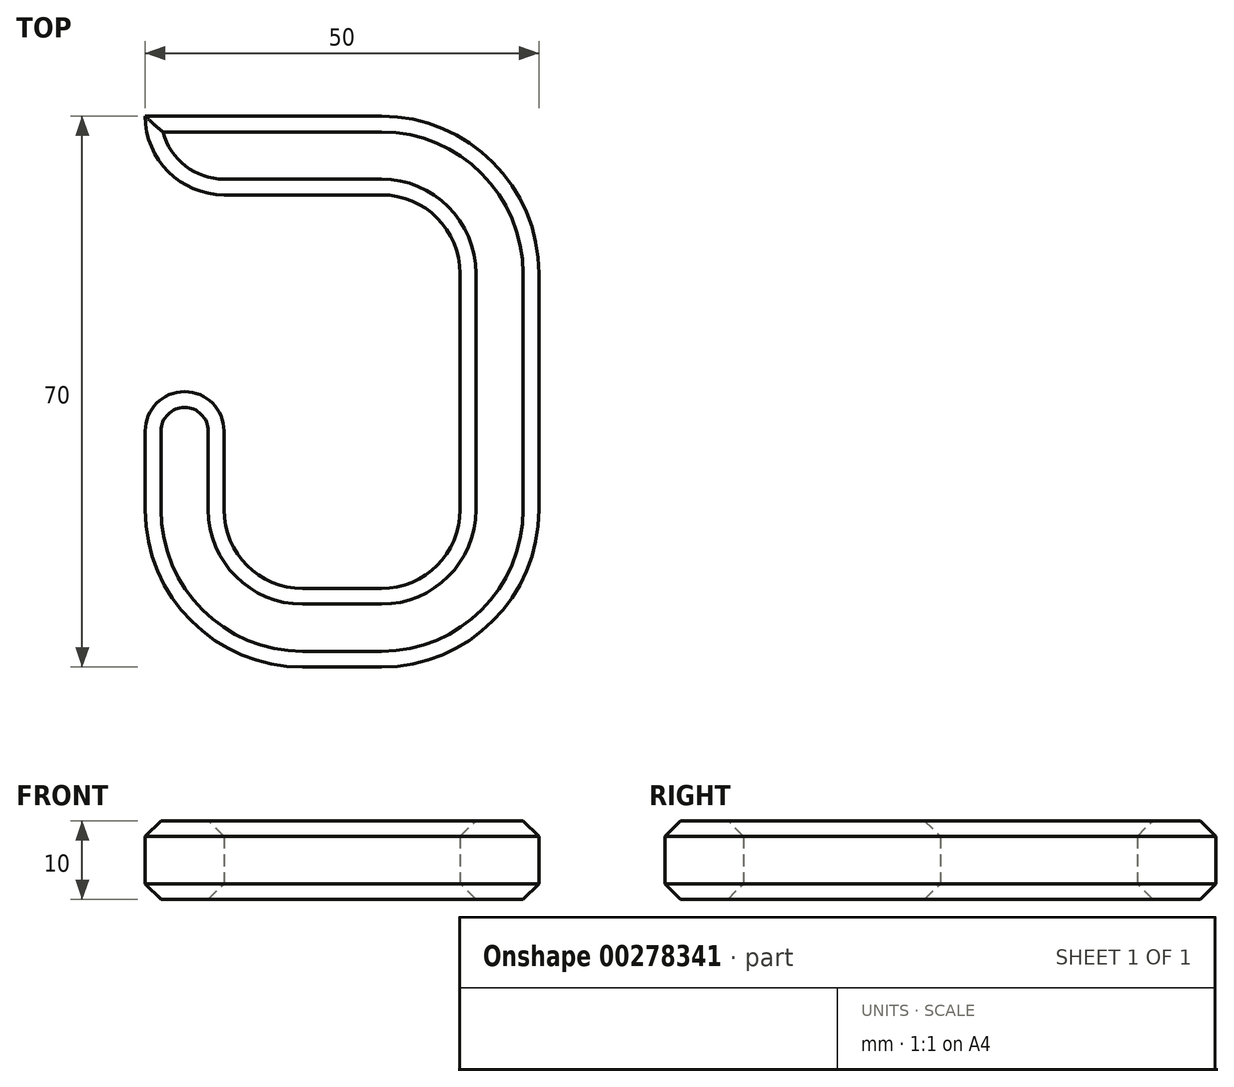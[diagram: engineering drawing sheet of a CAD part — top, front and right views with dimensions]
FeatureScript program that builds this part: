
annotation { "Feature Type Name" : "Feature", "Feature Type Description" : "" }
export const myFeature = defineFeature(function(context is Context, id is Id, definition is map)
    precondition{}
    {
        {
            var Q0;
            Q0=qCreatedBy(makeId("Top.planeOp"),FACE);
            var sketch = newSketch(context, id + "F0", { "sketchPlane" : qUnion([Q0])});
            skLineSegment(sketch, "E0.bottom", {"start": v(-5, 25) * mm, "end": v(5, 25) * mm});
            skLineSegment(sketch, "E0.top", {"start": v(-5, -25) * mm, "end": v(5, -25) * mm});
            skLineSegment(sketch, "E0.left", {"start": v(-5, 25) * mm, "end": v(-5, -25) * mm});
            skLineSegment(sketch, "E0.right", {"start": v(5, 25) * mm, "end": v(5, -25) * mm});
            skPoint(sketch, "E0.middle", {"position": v(0, 0) * mm});
            skLineSegment(sketch, "E1.bottom", {"start": v(-45, 35) * mm, "end": v(5, 35) * mm});
            skLineSegment(sketch, "E1.top", {"start": v(-45, 25) * mm, "end": v(5, 25) * mm});
            skLineSegment(sketch, "E1.left", {"start": v(-45, 35) * mm, "end": v(-45, 25) * mm});
            skLineSegment(sketch, "E1.right", {"start": v(5, 35) * mm, "end": v(5, 25) * mm});
            skLineSegment(sketch, "E2.bottom", {"start": v(-45, -35) * mm, "end": v(5, -35) * mm});
            skLineSegment(sketch, "E2.top", {"start": v(-45, -25) * mm, "end": v(5, -25) * mm});
            skLineSegment(sketch, "E2.left", {"start": v(-45, -35) * mm, "end": v(-45, -25) * mm});
            skLineSegment(sketch, "E2.right", {"start": v(5, -35) * mm, "end": v(5, -25) * mm});
            skLineSegment(sketch, "E3.bottom", {"start": v(-45, 25) * mm, "end": v(-35, 25) * mm});
            skLineSegment(sketch, "E3.top", {"start": v(-45, 10) * mm, "end": v(-35, 10) * mm});
            skLineSegment(sketch, "E3.left", {"start": v(-45, 25) * mm, "end": v(-45, 10) * mm});
            skLineSegment(sketch, "E3.right", {"start": v(-35, 25) * mm, "end": v(-35, 10) * mm});
            skLineSegment(sketch, "E4.bottom", {"start": v(-45, 0) * mm, "end": v(-35, 0) * mm});
            skLineSegment(sketch, "E4.top", {"start": v(-45, -25) * mm, "end": v(-35, -25) * mm});
            skLineSegment(sketch, "E4.left", {"start": v(-45, 0) * mm, "end": v(-45, -25) * mm});
            skLineSegment(sketch, "E4.right", {"start": v(-35, 0) * mm, "end": v(-35, -25) * mm});
            skSolve(sketch);
        }
        {
            var Q0;
            Q0=makeQuery(id+"F0.imprint","IMPRINT",FACE,{"disambiguationData":[TD([[makeQuery(id+"F0.imprint","IMPRINT",EDGE,{"derivedFrom":sQuery(id+"F0.wireOp",EDGE,"E3.bottom")}),-1.0]])]});
            var Q1;
            Q1=makeQuery(id+"F0.imprint","IMPRINT",FACE,{"disambiguationData":[TD([[makeQuery(id+"F0.imprint","IMPRINT",EDGE,{"derivedFrom":sQuery(id+"F0.wireOp",EDGE,"E1.bottom")}),-1.0]])]});
            var Q2;
            {var subQ0=sQuery(id+"F0.wireOp",EDGE,"E0.left");Q2=makeQuery(id+"F0.imprint","IMPRINT",FACE,{"disambiguationData":[TD([[makeQuery(id+"F0.imprint","IMPRINT",EDGE,{"derivedFrom":subQ0}),1.0]])]});}
            var Q3;
            Q3=makeQuery(id+"F0.imprint","IMPRINT",FACE,{"disambiguationData":[TD([[makeQuery(id+"F0.imprint","IMPRINT",EDGE,{"derivedFrom":sQuery(id+"F0.wireOp",EDGE,"E2.bottom")}),1.0]])]});
            var Q4;
            Q4=makeQuery(id+"F0.imprint","IMPRINT",FACE,{"disambiguationData":[TD([[makeQuery(id+"F0.imprint","IMPRINT",EDGE,{"derivedFrom":sQuery(id+"F0.wireOp",EDGE,"E4.bottom")}),-1.0]])]});
            extrude(context, id + "F1", {"entities" : qUnion([Q0, Q1, Q2, Q3, Q4]), "depth" : 10 * mm});
        }
        {
            var Q0;
            Q0=makeQuery(id+"F1.opExtrude","SWEPT_EDGE",EDGE,{"disambiguationData":[OSD([sQuery(id+"F0.wireOp",EDGE,"E1.top"),sQuery(id+"F0.wireOp",EDGE,"E3.bottom"),sQuery(id+"F0.wireOp",EDGE,"E3.right")])]});
            var Q1;
            Q1=makeQuery(id+"F1.opExtrude","SWEPT_EDGE",EDGE,{"disambiguationData":[OSD([sQuery(id+"F0.wireOp",EDGE,"E0.left"),sQuery(id+"F0.wireOp",EDGE,"E1.top")])]});
            var Q2;
            Q2=makeQuery(id+"F1.opExtrude","SWEPT_EDGE",EDGE,{"disambiguationData":[OSD([sQuery(id+"F0.wireOp",EDGE,"E0.left"),sQuery(id+"F0.wireOp",EDGE,"E2.top")])]});
            var Q3;
            Q3=makeQuery(id+"F1.opExtrude","SWEPT_EDGE",EDGE,{"disambiguationData":[OSD([sQuery(id+"F0.wireOp",EDGE,"E2.top"),sQuery(id+"F0.wireOp",EDGE,"E4.top"),sQuery(id+"F0.wireOp",EDGE,"E4.right")])]});
            fillet(context, id + "F2", {"entities" : qUnion([Q0, Q1, Q2, Q3]), "radius" : 10 * mm, "tangentPropagation" : true, "allowEdgeOverflow" : false});
        }
        {
            var Q0;
            Q0=makeQuery(id+"F1.opExtrude","SWEPT_EDGE",EDGE,{"disambiguationData":[OSD([sQuery(id+"F0.wireOp",EDGE,"E1.bottom"),sQuery(id+"F0.wireOp",EDGE,"E1.right")])]});
            var Q1;
            Q1=makeQuery(id+"F1.opExtrude","SWEPT_EDGE",EDGE,{"disambiguationData":[OSD([sQuery(id+"F0.wireOp",EDGE,"E1.bottom"),sQuery(id+"F0.wireOp",EDGE,"E1.left")])]});
            var Q2;
            Q2=makeQuery(id+"F1.opExtrude","SWEPT_EDGE",EDGE,{"disambiguationData":[OSD([sQuery(id+"F0.wireOp",EDGE,"E2.bottom"),sQuery(id+"F0.wireOp",EDGE,"E2.right")])]});
            var Q3;
            Q3=makeQuery(id+"F1.opExtrude","SWEPT_EDGE",EDGE,{"disambiguationData":[OSD([sQuery(id+"F0.wireOp",EDGE,"E2.bottom"),sQuery(id+"F0.wireOp",EDGE,"E2.left")])]});
            fillet(context, id + "F3", {"entities" : qUnion([Q0, Q1, Q2, Q3]), "radius" : 20 * mm, "tangentPropagation" : true, "allowEdgeOverflow" : false});
        }
        {
            var Q0;
            Q0=makeQuery(id+"F1.opExtrude","SWEPT_EDGE",EDGE,{"disambiguationData":[OSD([sQuery(id+"F0.wireOp",EDGE,"E3.top"),sQuery(id+"F0.wireOp",EDGE,"E3.right")])]});
            var Q1;
            Q1=makeQuery(id+"F1.opExtrude","SWEPT_EDGE",EDGE,{"disambiguationData":[OSD([sQuery(id+"F0.wireOp",EDGE,"E3.top"),sQuery(id+"F0.wireOp",EDGE,"E3.left")])]});
            var Q2;
            Q2=makeQuery(id+"F1.opExtrude","SWEPT_EDGE",EDGE,{"disambiguationData":[OSD([sQuery(id+"F0.wireOp",EDGE,"E4.bottom"),sQuery(id+"F0.wireOp",EDGE,"E4.left")])]});
            var Q3;
            Q3=makeQuery(id+"F1.opExtrude","SWEPT_EDGE",EDGE,{"disambiguationData":[OSD([sQuery(id+"F0.wireOp",EDGE,"E4.bottom"),sQuery(id+"F0.wireOp",EDGE,"E4.right")])]});
            fillet(context, id + "F4", {"entities" : qUnion([Q0, Q1, Q2, Q3]), "radius" : 5 * mm, "tangentPropagation" : true, "allowEdgeOverflow" : false});
        }
        {
            var Q0;
            Q0=makeQuery(id+"F1.opExtrude","CAP_EDGE",EDGE,{"disambiguationData":[OSD([sQuery(id+"F0.wireOp",EDGE,"E2.left"),sQuery(id+"F0.wireOp",EDGE,"E4.left")])],"isStart":true});
            var Q1;
            {var subQ0=sQuery(id+"F0.wireOp",EDGE,"E2.left");var subQ1=sQuery(id+"F0.wireOp",EDGE,"E2.bottom");Q1=makeQuery(id+"F3.opFillet","BLEND_EDGE",EDGE,{"blendedFrom":[makeQuery(id+"F1.opExtrude","SWEPT_EDGE",EDGE,{"disambiguationData":[OSD([subQ1,subQ0])]}),makeQuery(id+"F1.opExtrude","CAP_FACE",FACE,{"disambiguationData":[OSD([sQuery(id+"F0.wireOp",EDGE,"E0.left"),sQuery(id+"F0.wireOp",EDGE,"E0.right"),sQuery(id+"F0.wireOp",EDGE,"E1.bottom"),sQuery(id+"F0.wireOp",EDGE,"E1.top"),sQuery(id+"F0.wireOp",EDGE,"E1.left"),sQuery(id+"F0.wireOp",EDGE,"E1.right"),subQ1,sQuery(id+"F0.wireOp",EDGE,"E2.top"),subQ0,sQuery(id+"F0.wireOp",EDGE,"E2.right"),sQuery(id+"F0.wireOp",EDGE,"E3.top"),sQuery(id+"F0.wireOp",EDGE,"E3.left"),sQuery(id+"F0.wireOp",EDGE,"E3.right"),sQuery(id+"F0.wireOp",EDGE,"E4.bottom"),sQuery(id+"F0.wireOp",EDGE,"E4.left"),sQuery(id+"F0.wireOp",EDGE,"E4.right")])],"isStart":false})],"blendedInto":[makeQuery(id+"F1.opExtrude","CAP_FACE",FACE,{"disambiguationData":[OSD([sQuery(id+"F0.wireOp",EDGE,"E0.left"),sQuery(id+"F0.wireOp",EDGE,"E0.right"),sQuery(id+"F0.wireOp",EDGE,"E1.bottom"),sQuery(id+"F0.wireOp",EDGE,"E1.top"),sQuery(id+"F0.wireOp",EDGE,"E1.left"),sQuery(id+"F0.wireOp",EDGE,"E1.right"),subQ1,sQuery(id+"F0.wireOp",EDGE,"E2.top"),subQ0,sQuery(id+"F0.wireOp",EDGE,"E2.right"),sQuery(id+"F0.wireOp",EDGE,"E3.top"),sQuery(id+"F0.wireOp",EDGE,"E3.left"),sQuery(id+"F0.wireOp",EDGE,"E3.right"),sQuery(id+"F0.wireOp",EDGE,"E4.bottom"),sQuery(id+"F0.wireOp",EDGE,"E4.left"),sQuery(id+"F0.wireOp",EDGE,"E4.right")])],"isStart":false})]});}
            chamfer(context, id + "F5", {"entities" : qUnion([Q0, Q1]), "width" : 2 * mm, "tangentPropagation" : true});
        }
    });
